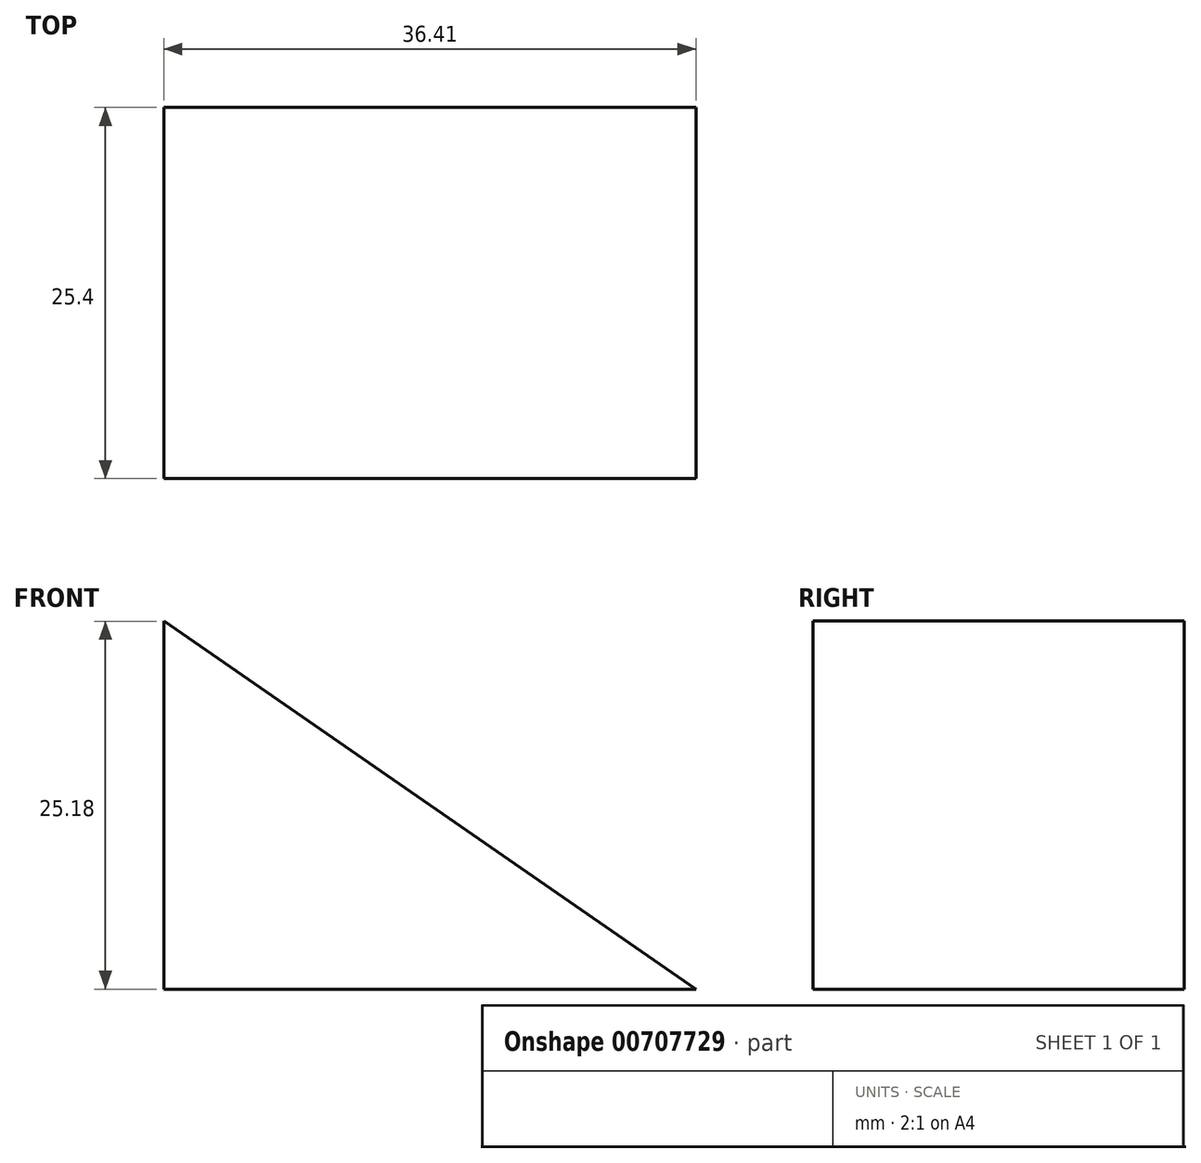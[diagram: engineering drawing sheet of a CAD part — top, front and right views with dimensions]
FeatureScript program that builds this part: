
annotation { "Feature Type Name" : "Feature", "Feature Type Description" : "" }
export const myFeature = defineFeature(function(context is Context, id is Id, definition is map)
    precondition{}
    {
        {
            var Q0;
            Q0=qCreatedBy(makeId("Front.planeOp"),FACE);
            var sketch = newSketch(context, id + "F0", { "sketchPlane" : qUnion([Q0])});
            skLineSegment(sketch, "E0", {"start": v(0, 0) * mm, "end": v(36.4, 0) * mm});
            skLineSegment(sketch, "E1", {"start": v(36.4, 0) * mm, "end": v(0, 25.18) * mm});
            skLineSegment(sketch, "E2", {"start": v(0, 25.18) * mm, "end": v(0, 0) * mm});
            skSolve(sketch);
        }
        {
            var Q0;
            Q0 = qSketchRegion(id + "F0", true);
            extrude(context, id + "F1", {"entities" : qUnion([Q0]), "depth" : 25.4 * mm, "offsetDistance" : 25.4 * mm});
        }
    });
